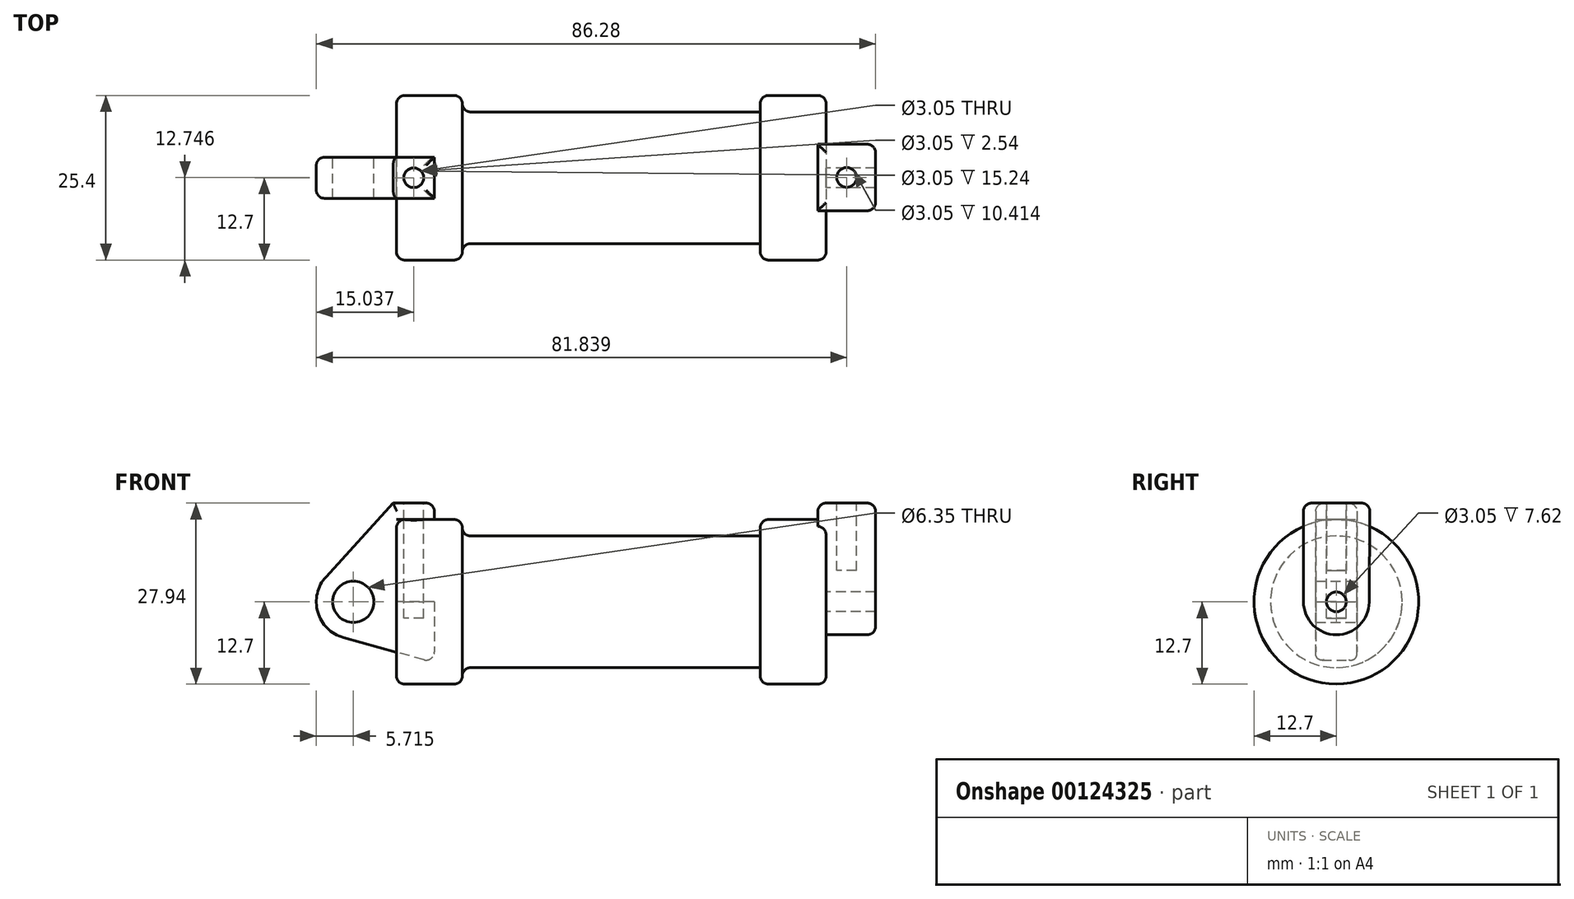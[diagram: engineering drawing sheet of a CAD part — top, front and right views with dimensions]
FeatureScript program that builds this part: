
annotation { "Feature Type Name" : "Feature", "Feature Type Description" : "" }
export const myFeature = defineFeature(function(context is Context, id is Id, definition is map)
    precondition{}
    {
        {
            var Q0;
            Q0=qCreatedBy(makeId("Front.planeOp"),FACE);
            var sketch = newSketch(context, id + "F0", { "sketchPlane" : qUnion([Q0])});
            skLineSegment(sketch, "E0", {"start": v(0, 0) * mm, "end": v(0, 12.7) * mm});
            skLineSegment(sketch, "E1", {"start": v(0, 12.7) * mm, "end": v(10.16, 12.7) * mm});
            skLineSegment(sketch, "E2", {"start": v(10.16, 12.7) * mm, "end": v(10.16, 10.16) * mm});
            skLineSegment(sketch, "E3", {"start": v(10.16, 10.16) * mm, "end": v(56.13, 10.16) * mm});
            skLineSegment(sketch, "E4", {"start": v(56.13, 10.16) * mm, "end": v(56.13, 12.7) * mm});
            skLineSegment(sketch, "E5", {"start": v(56.13, 12.7) * mm, "end": v(66.3, 12.7) * mm});
            skLineSegment(sketch, "E6", {"start": v(66.3, 12.7) * mm, "end": v(66.3, 0) * mm});
            skLineSegment(sketch, "E7", {"start": v(66.3, 0) * mm, "end": v(0, 0) * mm});
            skLineSegment(sketch, "E8", {"start": v(5.84, 15.24) * mm, "end": v(-0.5, 15.24) * mm});
            skLineSegment(sketch, "E9", {"start": v(-0.5, 15.24) * mm, "end": v(-10.88, 3.85) * mm});
            skLineSegment(sketch, "E10", {"start": v(0, 0) * mm, "end": v(-6.65, 0) * mm});
            skCircle(sketch, "E11", {"center": v(-6.65, 0) * mm, "radius": 5.72 * mm});
            skCircle(sketch, "E12", {"center": v(-6.65, 0) * mm, "radius": 3.18 * mm});
            skLineSegment(sketch, "E13", {"start": v(5.84, 15.24) * mm, "end": v(5.84, -9.4) * mm});
            skLineSegment(sketch, "E14", {"start": v(5.84, -9.4) * mm, "end": v(-8.18, -5.5) * mm});
            skSolve(sketch);
        }
        {
            var Q0;
            {var subQ0=sQuery(id+"F0.wireOp",EDGE,"E2");Q0=makeQuery(id+"F0.imprint","IMPRINT",FACE,{"disambiguationData":[TD([[makeQuery(id+"F0.imprint","IMPRINT",EDGE,{"derivedFrom":subQ0}),-1.0]])]});}
            var Q1;
            {var subQ0=sQuery(id+"F0.wireOp",EDGE,"E0");Q1=makeQuery(id+"F0.imprint","IMPRINT",FACE,{"disambiguationData":[TD([[makeQuery(id+"F0.imprint","IMPRINT",EDGE,{"derivedFrom":subQ0}),-1.0]])]});}
            var Q2;
            Q2=sQuery(id+"F0.wireOp",EDGE,"E7");
            revolve(context, id + "F1", {"entities" : qUnion([Q0, Q1]), "axis" : qUnion([Q2]), "revolveType" : RevolveType.FULL});
        }
        {
            var Q0;
            {var subQ0=sQuery(id+"F0.wireOp",EDGE,"E14");Q0=makeQuery(id+"F0.imprint","IMPRINT",FACE,{"disambiguationData":[TD([[makeQuery(id+"F0.imprint","IMPRINT",EDGE,{"derivedFrom":subQ0}),-1.0]])]});}
            var Q1;
            {var subQ4=sQuery(id+"F0.wireOp",EDGE,"E12");Q1=makeQuery(id+"F0.imprint","IMPRINT",FACE,{"disambiguationData":[TD([[makeQuery(id+"F0.imprint","IMPRINT",EDGE,{"derivedFrom":subQ4}),-1.0]])]});}
            var Q2;
            {var subQ3=sQuery(id+"F0.wireOp",EDGE,"E0");Q2=makeQuery(id+"F0.imprint","IMPRINT",FACE,{"disambiguationData":[TD([[makeQuery(id+"F0.imprint","IMPRINT",EDGE,{"derivedFrom":subQ3}),1.0]])]});}
            extrude(context, id + "F2", {"entities" : qUnion([Q0, Q1, Q2]), "endBound" : BoundingType.SYMMETRIC, "depth" : 6.35 * mm});
        }
        {
            var Q0;
            Q0=makeQuery(id+"F1.opRevolve","SWEPT_FACE",FACE,{"disambiguationData":[OSD([sQuery(id+"F0.wireOp",EDGE,"E6")])]});
            var sketch = newSketch(context, id + "F3", { "sketchPlane" : qUnion([Q0])});
            skCircle(sketch, "E15", {"center": v(0, 0) * mm, "radius": 1.52 * mm});
            skCircle(sketch, "E16", {"center": v(0, 0) * mm, "radius": 5.08 * mm});
            skLineSegment(sketch, "E17", {"start": v(-5.08, 0) * mm, "end": v(-5.08, 15.24) * mm});
            skLineSegment(sketch, "E18", {"start": v(-5.08, 15.24) * mm, "end": v(5.17, 15.24) * mm});
            skLineSegment(sketch, "E19", {"start": v(5.08, -0.03) * mm, "end": v(5.17, 15.24) * mm});
            skSolve(sketch);
        }
        {
            var Q0;
            {var subQ0=sQuery(id+"F3.wireOp",EDGE,"E17");var subQ1=sQuery(id+"F3.wireOp",EDGE,"E16");var subQ2=makeQuery(id+"F3.imprint","INTERSECT",VERTEX,{"derivedFrom":[subQ1,subQ0]});Q0=makeQuery(id+"F3.imprint","IMPRINT",FACE,{"disambiguationData":[TD([[makeQuery(id+"F3.imprint","IMPRINT",EDGE,{"disambiguationData":[TD([[subQ2,1.0]])],"derivedFrom":subQ1}),-1.0]])]});}
            var Q1;
            Q1=makeQuery(id+"F3.imprint","IMPRINT",FACE,{"disambiguationData":[TD([[makeQuery(id+"F3.imprint","IMPRINT",EDGE,{"derivedFrom":sQuery(id+"F3.wireOp",EDGE,"E15")}),-1.0]])]});
            var Q2;
            {var subQ0=sQuery(id+"F3.wireOp",EDGE,"E18");Q2=makeQuery(id+"F3.imprint","IMPRINT",FACE,{"disambiguationData":[TD([[makeQuery(id+"F3.imprint","IMPRINT",EDGE,{"derivedFrom":subQ0}),-1.0]])]});}
            extrude(context, id + "F4", {"entities" : qUnion([Q0, Q1, Q2]), "operationType" : NewBodyOperationType.ADD, "depth" : 7.62 * mm, "hasSecondDirection" : true, "secondDirectionOppositeDirection" : true, "secondDirectionDepth" : 1.27 * mm});
        }
        {
            var Q0;
            Q0=makeQuery(id+"F2.opExtrude","SWEPT_FACE",FACE,{"disambiguationData":[OSD([sQuery(id+"F0.wireOp",EDGE,"E8")])]});
            var sketch = newSketch(context, id + "F5", { "sketchPlane" : qUnion([Q0])});
            skCircle(sketch, "E20", {"center": v(2.67, 0) * mm, "radius": 1.52 * mm});
            skSolve(sketch);
        }
        {
            var Q0;
            Q0 = qSketchRegion(id + "F5", true);
            extrude(context, id + "F6", {"entities" : qUnion([Q0]), "operationType" : NewBodyOperationType.REMOVE, "oppositeDirection" : true, "depth" : 17.78 * mm});
        }
        {
            var Q0;
            Q0=makeQuery(id+"F4.opExtrude","SWEPT_FACE",FACE,{"disambiguationData":[OSD([sQuery(id+"F3.wireOp",EDGE,"E18")])]});
            var sketch = newSketch(context, id + "F7", { "sketchPlane" : qUnion([Q0])});
            skCircle(sketch, "E21", {"center": v(69.47, 0.05) * mm, "radius": 1.52 * mm});
            skSolve(sketch);
        }
        {
            var Q0;
            Q0=makeQuery(id+"F7.imprint","IMPRINT",FACE,{"disambiguationData":[TD([[makeQuery(id+"F7.imprint","IMPRINT",EDGE,{"derivedFrom":sQuery(id+"F7.wireOp",EDGE,"E21")}),1.0]])]});
            extrude(context, id + "F8", {"entities" : qUnion([Q0]), "operationType" : NewBodyOperationType.REMOVE, "oppositeDirection" : true, "depth" : 10.4 * mm});
        }
        {
            var Q0;
            Q0=makeQuery(id+"F1.opRevolve","SWEPT_EDGE",EDGE,{"disambiguationData":[OSD([sQuery(id+"F0.wireOp",EDGE,"E5"),sQuery(id+"F0.wireOp",EDGE,"E6")])]});
            var Q1;
            Q1=makeQuery(id+"F1.opRevolve","SWEPT_EDGE",EDGE,{"disambiguationData":[OSD([sQuery(id+"F0.wireOp",EDGE,"E1"),sQuery(id+"F0.wireOp",EDGE,"E2")])]});
            var Q2;
            Q2=makeQuery(id+"F1.opRevolve","SWEPT_EDGE",EDGE,{"disambiguationData":[OSD([sQuery(id+"F0.wireOp",EDGE,"E0"),sQuery(id+"F0.wireOp",EDGE,"E1")])]});
            var Q3;
            Q3=makeQuery(id+"F4.opExtrude","SWEPT_EDGE",EDGE,{"disambiguationData":[OSD([sQuery(id+"F3.wireOp",EDGE,"E18"),sQuery(id+"F3.wireOp",EDGE,"E19")])]});
            var Q4;
            Q4=makeQuery(id+"F4.opExtrude","CAP_EDGE",EDGE,{"disambiguationData":[OSD([sQuery(id+"F3.wireOp",EDGE,"E16")])],"isStart":false});
            var Q5;
            Q5=makeQuery(id+"F4.opExtrude","CAP_EDGE",EDGE,{"disambiguationData":[OSD([sQuery(id+"F3.wireOp",EDGE,"E18")])],"isStart":false});
            var Q6;
            Q6=makeQuery(id+"F2.opExtrude","SWEPT_EDGE",EDGE,{"disambiguationData":[OSD([sQuery(id+"F0.wireOp",EDGE,"E8"),sQuery(id+"F0.wireOp",EDGE,"E13")])]});
            var Q7;
            Q7=makeQuery(id+"F2.opExtrude","CAP_EDGE",EDGE,{"disambiguationData":[OSD([sQuery(id+"F0.wireOp",EDGE,"E8")])],"isStart":true});
            var Q8;
            Q8=makeQuery(id+"F2.opExtrude","CAP_EDGE",EDGE,{"disambiguationData":[OSD([sQuery(id+"F0.wireOp",EDGE,"E9")])],"isStart":true});
            var Q9;
            Q9=makeQuery(id+"F2.opExtrude","CAP_EDGE",EDGE,{"disambiguationData":[OSD([sQuery(id+"F0.wireOp",EDGE,"E11")])],"isStart":true});
            var Q10;
            Q10=makeQuery(id+"F4.opExtrude","SWEPT_EDGE",EDGE,{"disambiguationData":[OSD([sQuery(id+"F3.wireOp",EDGE,"E17"),sQuery(id+"F3.wireOp",EDGE,"E18")])]});
            var Q11;
            Q11=makeQuery(id+"F2.opExtrude","CAP_EDGE",EDGE,{"disambiguationData":[OSD([sQuery(id+"F0.wireOp",EDGE,"E9")])],"isStart":false});
            var Q12;
            Q12=makeQuery(id+"F2.opExtrude","CAP_EDGE",EDGE,{"disambiguationData":[OSD([sQuery(id+"F0.wireOp",EDGE,"E11")])],"isStart":false});
            var Q13;
            Q13=makeQuery(id+"F2.opExtrude","CAP_EDGE",EDGE,{"disambiguationData":[OSD([sQuery(id+"F0.wireOp",EDGE,"E14")])],"isStart":false});
            var Q14;
            Q14=makeQuery(id+"F2.opExtrude","CAP_EDGE",EDGE,{"disambiguationData":[OSD([sQuery(id+"F0.wireOp",EDGE,"E14")])],"isStart":true});
            var Q15;
            Q15=makeQuery(id+"F2.opExtrude","SWEPT_FACE",FACE,{"disambiguationData":[OSD([sQuery(id+"F0.wireOp",EDGE,"E14")])]});
            var Q16;
            Q16=makeQuery(id+"F2.opExtrude","CAP_EDGE",EDGE,{"disambiguationData":[OSD([sQuery(id+"F0.wireOp",EDGE,"E8")])],"isStart":false});
            var Q17;
            Q17=makeQuery(id+"F4.opExtrude","CAP_EDGE",EDGE,{"disambiguationData":[OSD([sQuery(id+"F3.wireOp",EDGE,"E18")])],"isStart":true});
            var Q18;
            Q18=makeQuery(id+"F1.opRevolve","SWEPT_EDGE",EDGE,{"disambiguationData":[OSD([sQuery(id+"F0.wireOp",EDGE,"E2"),sQuery(id+"F0.wireOp",EDGE,"E3")])]});
            var Q19;
            Q19=makeQuery(id+"F1.opRevolve","SWEPT_EDGE",EDGE,{"disambiguationData":[OSD([sQuery(id+"F0.wireOp",EDGE,"E4"),sQuery(id+"F0.wireOp",EDGE,"E5")])]});
            fillet(context, id + "F9", {"entities" : qUnion([Q0, Q1, Q2, Q3, Q4, Q5, Q6, Q7, Q8, Q9, Q10, Q11, Q12, Q13, Q14, Q15, Q16, Q17, Q18, Q19]), "radius" : 1.27 * mm, "tangentPropagation" : true, "allowEdgeOverflow" : false});
        }
    });
